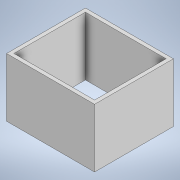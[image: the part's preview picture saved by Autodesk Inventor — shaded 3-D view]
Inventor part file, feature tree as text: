
AUTODESK INVENTOR PART (.ipt)
format: ipt  version: 2022.1 (Build 261234000, 234)  size: 97,280 bytes
history: native  units: in
note: dims shown in document units (in); Inventor stores cm internally (conversion verified against a paired STEP export)
features: extrude x1, sketch x1
ambient origin geometry x8: Origin, YZ Plane, XZ Plane, XY Plane, X Axis, Y Axis, Z Axis, Center Point
bodies: Solid1 (feature_tree)
feature tree (2):
  extrude  "Extrusion1"  Depth=3.0in
  sketch  "Sketch1"  dims[d0=2.6875in d1=3.0in d2=0.125in d3=0.125in d4=2.0in d5=0.0in]
